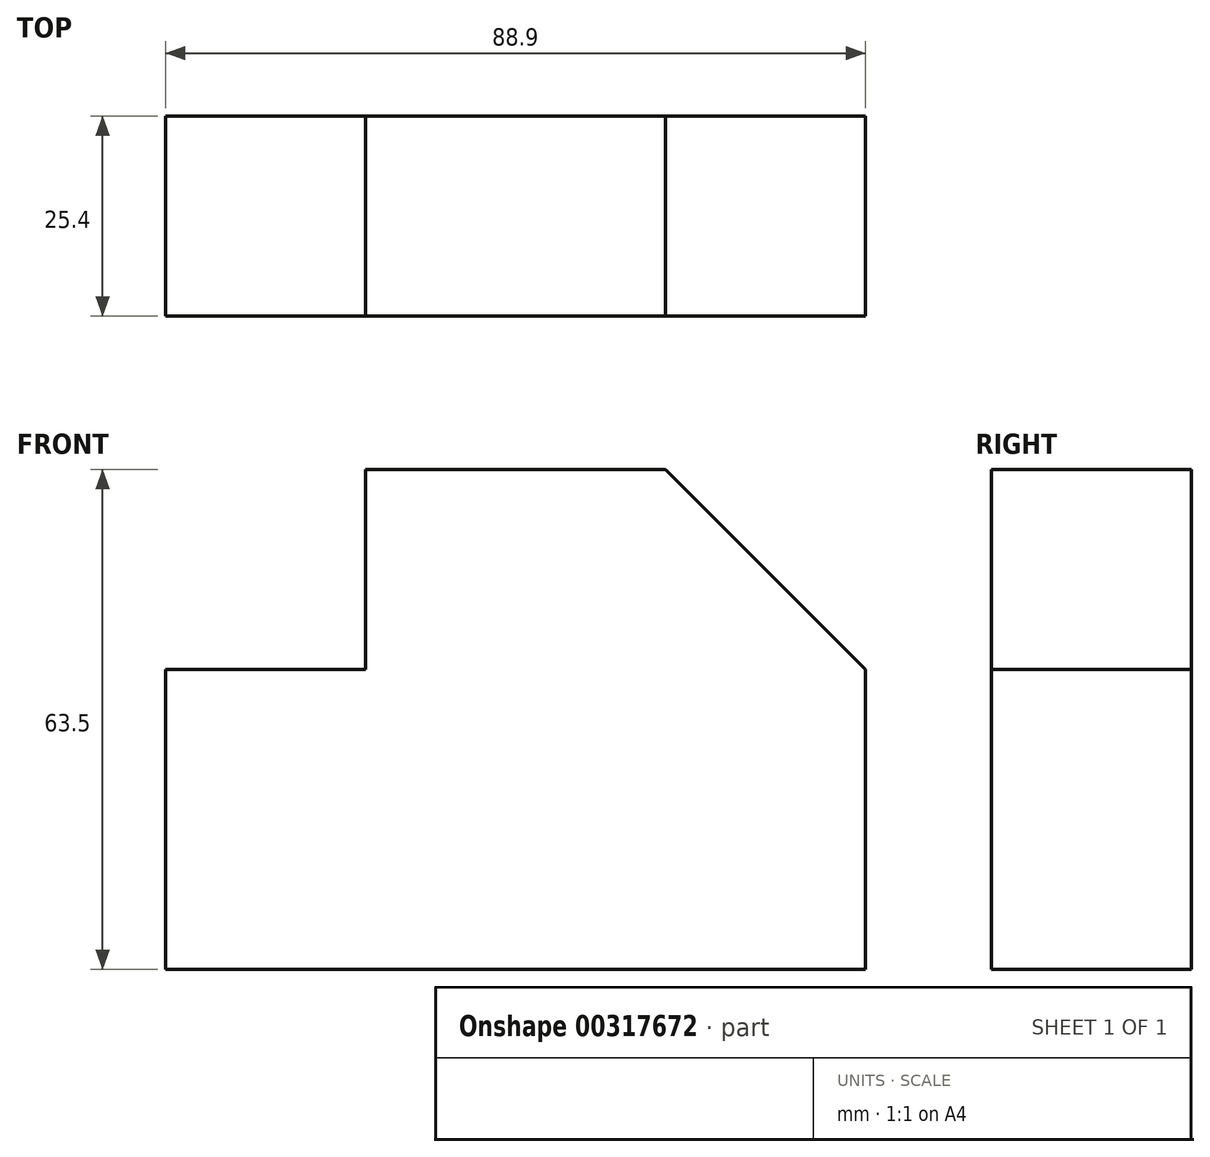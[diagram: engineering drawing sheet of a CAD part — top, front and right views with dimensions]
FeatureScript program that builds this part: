
annotation { "Feature Type Name" : "Feature", "Feature Type Description" : "" }
export const myFeature = defineFeature(function(context is Context, id is Id, definition is map)
    precondition{}
    {
        {
            var Q0;
            Q0=qCreatedBy(makeId("Front.planeOp"),FACE);
            var sketch = newSketch(context, id + "F0", { "sketchPlane" : qUnion([Q0])});
            skLineSegment(sketch, "E0", {"start": v(-44.3, -37.98) * mm, "end": v(44.6, -37.98) * mm});
            skLineSegment(sketch, "E1", {"start": v(44.6, -37.98) * mm, "end": v(44.6, 0.12) * mm});
            skLineSegment(sketch, "E2", {"start": v(-44.3, -37.98) * mm, "end": v(-44.3, 0.12) * mm});
            skLineSegment(sketch, "E3", {"start": v(-44.3, 0.12) * mm, "end": v(-18.9, 0.12) * mm});
            skLineSegment(sketch, "E4", {"start": v(-18.9, 0.12) * mm, "end": v(-18.9, 25.52) * mm});
            skLineSegment(sketch, "E5", {"start": v(-18.9, 25.52) * mm, "end": v(19.2, 25.52) * mm});
            skLineSegment(sketch, "E6", {"start": v(19.2, 25.52) * mm, "end": v(44.6, 0.12) * mm});
            skSolve(sketch);
        }
        {
            var Q0;
            Q0 = qSketchRegion(id + "F0", true);
            extrude(context, id + "F1", {"entities" : qUnion([Q0]), "depth" : 25.4 * mm});
        }
    });
